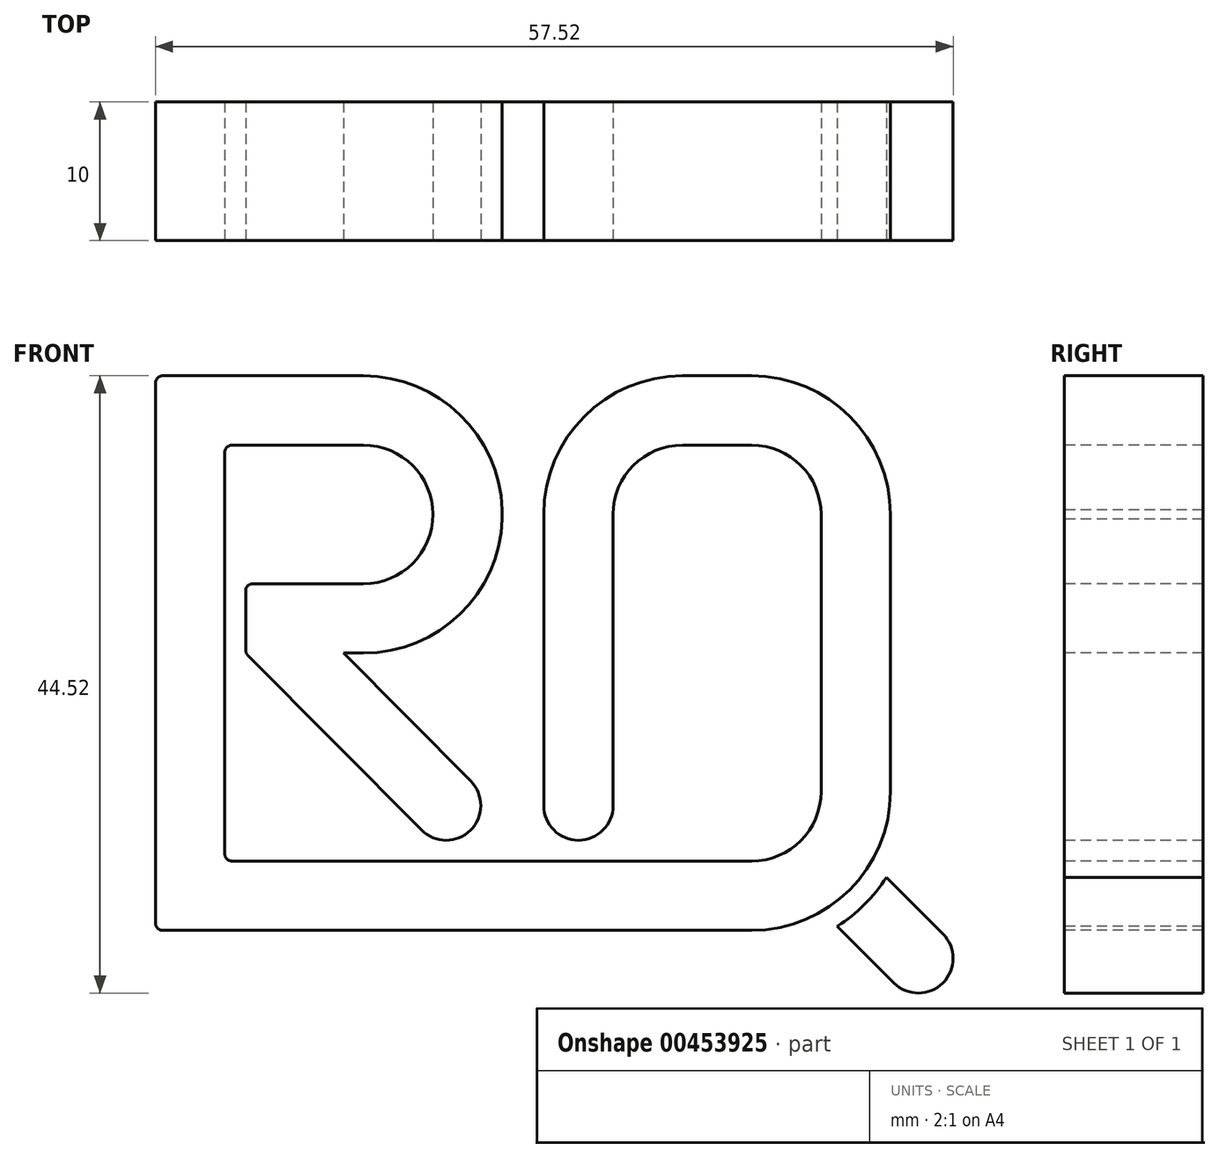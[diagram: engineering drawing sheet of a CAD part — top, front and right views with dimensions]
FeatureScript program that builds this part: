
annotation { "Feature Type Name" : "Feature", "Feature Type Description" : "" }
export const myFeature = defineFeature(function(context is Context, id is Id, definition is map)
    precondition{}
    {
        {
            var Q0;
            Q0=qCreatedBy(makeId("Front.planeOp"),FACE);
            var sketch = newSketch(context, id + "F0", { "sketchPlane" : qUnion([Q0])});
            skLineSegment(sketch, "E0.bottom", {"start": v(23, -20) * mm, "end": v(19.46, -20) * mm});
            skPoint(sketch, "E0.middle", {"position": v(0, 0) * mm});
            skLineSegment(sketch, "E1", {"start": v(-25, 14.5) * mm, "end": v(-25, -14.5) * mm});
            skLineSegment(sketch, "E2", {"start": v(-2, -20) * mm, "end": v(-0.38, -20) * mm});
            skLineSegment(sketch, "E3", {"start": v(-2, -11) * mm, "end": v(-2, 10) * mm});
            skLineSegment(sketch, "E4", {"start": v(8, 20) * mm, "end": v(13, 20) * mm});
            skLineSegment(sketch, "E5", {"start": v(23, 10) * mm, "end": v(23, -10) * mm});
            skLineSegment(sketch, "E6", {"start": v(13, -20) * mm, "end": v(9, -20) * mm});
            skLineSegment(sketch, "E7", {"start": v(-25, 20) * mm, "end": v(-15, 20) * mm});
            skLineSegment(sketch, "E8", {"start": v(-23.5, 0) * mm, "end": v(-15, 0) * mm});
            skLineSegment(sketch, "E9", {"start": v(-23.35, -0.15) * mm, "end": v(-10.82, -12.76) * mm});
            skLineSegment(sketch, "E10", {"start": v(-5, 10.33) * mm, "end": v(-5, 10.33) * mm});
            skPoint(sketch, "E11.visualSharp", {"position": v(-5.33, 20) * mm});
            skArc(sketch, "E11.filletArc", {"start": v(-5, 10.33) * mm, "mid": v(-8.05, 17.19) * mm, "end": v(-15, 20) * mm});
            skArc(sketch, "E12.filletArc", {"start": v(-15, 0) * mm, "mid": v(-7.81, 3.05) * mm, "end": v(-5, 10.33) * mm});
            skPoint(sketch, "E13.visualSharp", {"position": v(-3.63, -20) * mm});
            skPoint(sketch, "E14.visualSharp", {"position": v(23, -20) * mm});
            skArc(sketch, "E14.filletArc", {"start": v(13, -20) * mm, "mid": v(20.07, -17.07) * mm, "end": v(23, -10) * mm});
            skPoint(sketch, "E15.visualSharp", {"position": v(23, 20) * mm});
            skArc(sketch, "E15.filletArc", {"start": v(23, 10) * mm, "mid": v(20.07, 17.07) * mm, "end": v(13, 20) * mm});
            skPoint(sketch, "E16.visualSharp", {"position": v(-2, 20) * mm});
            skArc(sketch, "E16.filletArc", {"start": v(8, 20) * mm, "mid": v(0.92, 17.07) * mm, "end": v(-2, 10) * mm});
            skPoint(sketch, "E17.visualSharp", {"position": v(-2, -20) * mm});
            skArc(sketch, "E18.0", {"start": v(8, 15) * mm, "mid": v(4.46, 13.54) * mm, "end": v(3, 10) * mm});
            skLineSegment(sketch, "E18.1", {"start": v(3, -11) * mm, "end": v(3, 10) * mm});
            skLineSegment(sketch, "E18.2", {"start": v(8, 15) * mm, "end": v(13, 15) * mm});
            skArc(sketch, "E18.4", {"start": v(18, 10) * mm, "mid": v(16.53, 13.54) * mm, "end": v(13, 15) * mm});
            skLineSegment(sketch, "E18.5", {"start": v(18, 10) * mm, "end": v(18, -10) * mm});
            skArc(sketch, "E18.6", {"start": v(13, -15) * mm, "mid": v(16.53, -13.54) * mm, "end": v(18, -10) * mm});
            skLineSegment(sketch, "E18.7", {"start": v(13, -15) * mm, "end": v(9, -15) * mm});
            skLineSegment(sketch, "E19.0", {"start": v(-23, 5) * mm, "end": v(-15, 5) * mm});
            skArc(sketch, "E19.1", {"start": v(-15, 5) * mm, "mid": v(-11.44, 6.5) * mm, "end": v(-10, 10.08) * mm});
            skArc(sketch, "E19.2", {"start": v(-10, 10.08) * mm, "mid": v(-11.5, 13.56) * mm, "end": v(-15, 15) * mm});
            skLineSegment(sketch, "E19.3", {"start": v(-24.5, 15) * mm, "end": v(-15, 15) * mm});
            skLineSegment(sketch, "E20.0", {"start": v(-30, 17.5) * mm, "end": v(-30, -19.5) * mm});
            skLineSegment(sketch, "E21.0", {"start": v(-1, -15) * mm, "end": v(-0.38, -15) * mm});
            skLineSegment(sketch, "E21.2", {"start": v(-16.58, 0.12) * mm, "end": v(-7.27, -9.24) * mm});
            skLineSegment(sketch, "E22", {"start": v(-23.5, 4.5) * mm, "end": v(-23.5, 0.2) * mm});
            skLineSegment(sketch, "E23", {"start": v(-29.5, -20) * mm, "end": v(-25, -20) * mm});
            skLineSegment(sketch, "E24", {"start": v(-25, -20) * mm, "end": v(-2, -20) * mm});
            skLineSegment(sketch, "E25", {"start": v(-1, -15) * mm, "end": v(9, -15) * mm});
            skLineSegment(sketch, "E26.0", {"start": v(-24.5, -15) * mm, "end": v(0, -15) * mm});
            skLineSegment(sketch, "E27", {"start": v(-5, 10.33) * mm, "end": v(-5, 0) * mm});
            skLineSegment(sketch, "E28", {"start": v(0.5, -13.5) * mm, "end": v(0.5, -13.5) * mm});
            skPoint(sketch, "E29.visualSharp", {"position": v(3, -13.5) * mm});
            skArc(sketch, "E29.filletArc", {"start": v(0.5, -13.5) * mm, "mid": v(2.26, -12.77) * mm, "end": v(3, -11) * mm});
            skPoint(sketch, "E30.newPointB", {"position": v(-23.5, -13.5) * mm});
            skArc(sketch, "E30.filletArc", {"start": v(-2, -11) * mm, "mid": v(-1.27, -12.77) * mm, "end": v(0.5, -13.5) * mm});
            skPoint(sketch, "E31.visualSharp", {"position": v(-30, -20) * mm});
            skArc(sketch, "E31.filletArc", {"start": v(-30, -19.5) * mm, "mid": v(-29.85, -19.85) * mm, "end": v(-29.5, -20) * mm});
            skLineSegment(sketch, "E32", {"start": v(-7.28, -12.77) * mm, "end": v(-7.28, -12.77) * mm});
            skArc(sketch, "E33.filletArc", {"start": v(-7.28, -12.77) * mm, "mid": v(-6.55, -11) * mm, "end": v(-7.27, -9.24) * mm});
            skArc(sketch, "E34.filletArc", {"start": v(-10.82, -12.76) * mm, "mid": v(-9.05, -13.5) * mm, "end": v(-7.28, -12.77) * mm});
            skLineSegment(sketch, "E35", {"start": v(21.13, -18.13) * mm, "end": v(24.99, -22) * mm});
            skLineSegment(sketch, "E36.0", {"start": v(19.16, -19.7) * mm, "end": v(23.25, -23.79) * mm});
            skLineSegment(sketch, "E37.0", {"start": v(22.7, -16.17) * mm, "end": v(26.78, -20.25) * mm});
            skLineSegment(sketch, "E38.0", {"start": v(14.76, -15.3) * mm, "end": v(14.29, -14.83) * mm});
            skPoint(sketch, "E39.newPointB", {"position": v(-25, 20) * mm});
            skArc(sketch, "E39.filletArc", {"start": v(-24.5, 15) * mm, "mid": v(-24.85, 14.85) * mm, "end": v(-25, 14.5) * mm});
            skPoint(sketch, "E40.visualSharp", {"position": v(-23.5, 5) * mm});
            skArc(sketch, "E40.filletArc", {"start": v(-23, 5) * mm, "mid": v(-23.35, 4.85) * mm, "end": v(-23.5, 4.5) * mm});
            skPoint(sketch, "E41.visualSharp", {"position": v(-23.5, 0) * mm});
            skArc(sketch, "E41.filletArc", {"start": v(-23.5, 0.2) * mm, "mid": v(-23.46, 0.02) * mm, "end": v(-23.35, -0.15) * mm});
            skLineSegment(sketch, "E42", {"start": v(-30, 17.5) * mm, "end": v(-30, 19.5) * mm});
            skLineSegment(sketch, "E43", {"start": v(-25, 20) * mm, "end": v(-29.5, 20) * mm});
            skPoint(sketch, "E44.visualSharp", {"position": v(-30, 20) * mm});
            skArc(sketch, "E44.filletArc", {"start": v(-29.5, 20) * mm, "mid": v(-29.85, 19.85) * mm, "end": v(-30, 19.5) * mm});
            skCircle(sketch, "E45", {"center": v(25.02, -22.02) * mm, "radius": 2.5 * mm});
            skPoint(sketch, "E46", {"position": v(20.07, -17.07) * mm});
            skArc(sketch, "E47.0", {"start": v(13, -21.5) * mm, "mid": v(15.93, -21.12) * mm, "end": v(18.67, -20) * mm});
            skPoint(sketch, "E48.orphan", {"position": v(16.53, -13.54) * mm});
            skLineSegment(sketch, "E49.trimOffspring", {"start": v(13, -20) * mm, "end": v(-0.38, -20) * mm});
            skArc(sketch, "E50.trimOffspring", {"start": v(19.16, -19.7) * mm, "mid": v(23.07, -15.54) * mm, "end": v(24.5, -10) * mm});
            skPoint(sketch, "E51.newPointB", {"position": v(-25, -20) * mm});
            skArc(sketch, "E51.filletArc", {"start": v(-25, -14.5) * mm, "mid": v(-24.85, -14.85) * mm, "end": v(-24.5, -15) * mm});
            skLineSegment(sketch, "E52", {"start": v(20.07, -17.07) * mm, "end": v(17.78, -19.35) * mm});
            skLineSegment(sketch, "E53.MirrorCS", {"start": v(17.43, -17.97) * mm, "end": v(13.35, -13.89) * mm});
            skSolve(sketch);
        }
        {
            var Q0;
            Q0=makeQuery(id+"F0.imprint","IMPRINT",FACE,{"disambiguationData":[TD([[makeQuery(id+"F0.imprint","IMPRINT",EDGE,{"derivedFrom":sQuery(id+"F0.wireOp",EDGE,"E1")}),-1.0]])]});
            var Q1;
            {var subQ6=sQuery(id+"F0.wireOp",EDGE,"E9");Q1=makeQuery(id+"F0.imprint","IMPRINT",FACE,{"disambiguationData":[TD([[makeQuery(id+"F0.imprint","IMPRINT",EDGE,{"derivedFrom":subQ6}),1.0]])]});}
            var Q2;
            {var subQ0=sQuery(id+"F0.wireOp",EDGE,"E45");var subQ1=makeQuery(id+"F0.imprint","INTERSECT",VERTEX,{"derivedFrom":[sQuery(id+"F0.wireOp",EDGE,"E37.0"),subQ0]});Q2=makeQuery(id+"F0.imprint","IMPRINT",FACE,{"disambiguationData":[TD([[makeQuery(id+"F0.imprint","IMPRINT",EDGE,{"disambiguationData":[TD([[subQ1,-1.0]])],"derivedFrom":subQ0}),1.0]])]});}
            var Q3;
            {var subQ1=sQuery(id+"F0.wireOp",EDGE,"E37.0");Q3=makeQuery(id+"F0.imprint","IMPRINT",FACE,{"disambiguationData":[TD([[makeQuery(id+"F0.imprint","IMPRINT",EDGE,{"derivedFrom":subQ1}),-1.0]])]});}
            var Q4;
            {var subQ0=sQuery(id+"F0.wireOp",EDGE,"E0.bottom");Q4=makeQuery(id+"F0.imprint","IMPRINT",FACE,{"disambiguationData":[TD([[makeQuery(id+"F0.imprint","IMPRINT",EDGE,{"derivedFrom":subQ0}),-1.0]])]});}
            var Q5;
            {var subQ0=sQuery(id+"F0.wireOp",EDGE,"E0.bottom");Q5=makeQuery(id+"F0.imprint","IMPRINT",FACE,{"disambiguationData":[TD([[makeQuery(id+"F0.imprint","IMPRINT",EDGE,{"derivedFrom":subQ0}),1.0]])]});}
            extrude(context, id + "F1", {"entities" : qUnion([Q0, Q1, Q2, Q3, Q4, Q5]), "oppositeDirection" : true, "depth" : 10 * mm});
        }
    });
